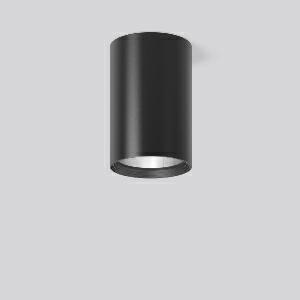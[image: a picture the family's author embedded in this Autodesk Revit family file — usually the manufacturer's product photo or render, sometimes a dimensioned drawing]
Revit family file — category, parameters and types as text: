
# Revit family: heledon_maxi_a_931219_003_2_cf3d
name_source: partatom
category: Lighting Fixtures
units: mm (PartAtom-declared; Revit-internal decimal feet)

## family parameters
Cut with Voids When Loaded = No
Host = Face
Light Source = No
Part Type = Normal
Room Calculation Point = No
Round Connector Dimension = Use Diameter
Shared = No

## types (1)
- HELEDON maxi A (1 x LED Modul 927, 3050 lm, 2700)
    Apparent Load = 25 VA
    Approval mark = CE
    CIE Flux Codes = 97 100 100 100 100
    Color Rendering = 92
    Color Temperature = 2700
    Default Elevation = 1800 mm
    Description = Series: HELEDON maxi
Cylindrical surface-mounted downlight. Housing: die-cast aluminium, powder-coated. Internal ceiling frame polycarbonate with bayonet mounting. Black plastic ring and recessed LED to prevent glare from the side. Optical assembly with reflector made of MIRO-Silver with 98% total light reflection for outstanding efficiency - can be changed without tools. Best colour rendering index Ra>90. Suitable for Ceiling mounting. Easy installation with a separate ceiling frame with bayonet mounting and plug connection. Driver integrated. Connected via plug-in connector. High quality converter without flickering and stroboscopic effect. The following accessories can be mounted without use of tools: interchangeable lenses, decorative glasses, honeycomb louvre, clear and frosted diffusers, white interchangeable plastic ring. 
Colour: deep black, matt (RAL 9005)
Diameter: 123 mm
Height: 183 mm
Lamp: LED
Socket: without socket
Colour temperature: 2700K
Colour rendering index (CRI): 92
System power: 25 W
Rated luminous flux: 3050 lm
Luminous efficiency: 122 lm/W
Control gear: Regulated power supply
Protection class: I
Type of protection: IP 20
    Height = 183 mm
    Lamp = 1 x LED Modul 927
    Lamp Light Flux = 3050 lm
    Lamp count = 1
    Length = 123 mm
    Lifetime = 50000 h
    Luminous efficacy = 122 lm/W
    Manufacturer = RZB
    ModVariant = No
    Model = 931219.003.2
    Mounting Place = Ceiling
    Mounting Type = Surface mounted
    Number of Poles = 1
    OnlyDefault = Yes
    Power Factor = 1
    Product Name = HELEDON maxi A
    Product group = Surface mounted downlights
    ProductGroupID = 302
    Protection Class = Protection class I
    Protection Degree = IP 20
    RLX_Detail_Level = 1
    RLX_Emergency_Light_Flux = 0 lm
    RLX_Emergency_Type = 0
    RLX_Emergency_Type_DB = No
    RlxData = <blob elided: 98317 chars, md5=f0722c00>
    Socket = socket
    Standby Power = 0 W
    System Light Flux = 3050 lm
    System Power = 25 W
    Type Comments = Product without accessories
    Type Image = 931192.003.jpg
    URL = http://relux.com
    VarID = ---
    Voltage = 230 V
    Voltage Range = 220-240 V
    Weight = 0.00 kg
    Width = 0 mm  [stored 0 ft]

note: [stored X ft] marks values corroborated as IEEE doubles in the binary element streams (Revit-internal decimal feet)

## geometry (parser evidence)
native form markers: Blend x4, Sweep x11
no freeform markers — native parametric forms only
